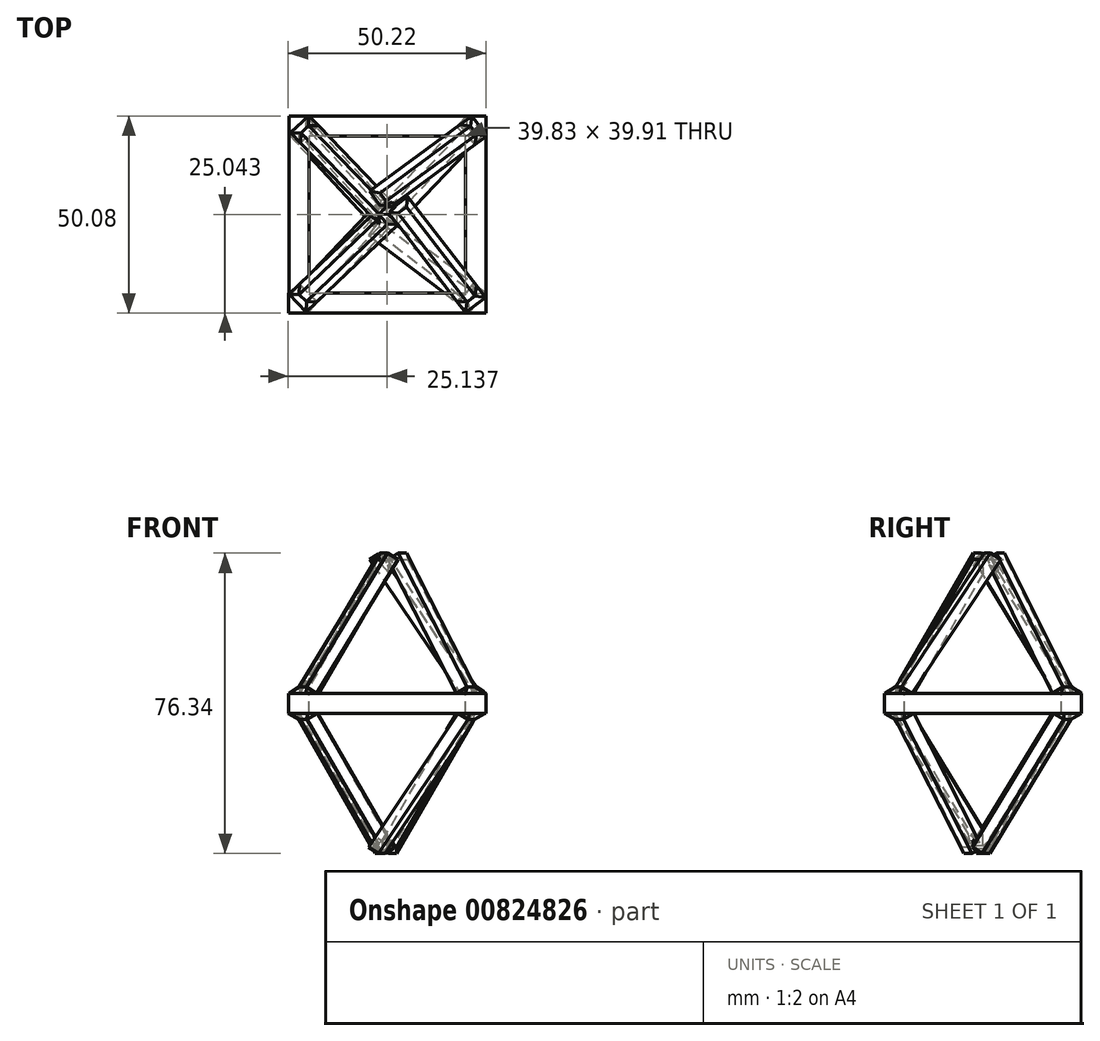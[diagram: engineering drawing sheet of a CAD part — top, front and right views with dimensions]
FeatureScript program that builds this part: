
annotation { "Feature Type Name" : "Feature", "Feature Type Description" : "" }
export const myFeature = defineFeature(function(context is Context, id is Id, definition is map)
    precondition{}
    {
        {
            var Q0;
            Q0=qCreatedBy(makeId("Top.planeOp"),FACE);
            var sketch = newSketch(context, id + "F0", { "sketchPlane" : qUnion([Q0])});
            skLineSegment(sketch, "E0.bottom", {"start": v(-22.5, 22.5) * mm, "end": v(22.5, 22.5) * mm});
            skLineSegment(sketch, "E0.top", {"start": v(-22.5, -22.5) * mm, "end": v(22.5, -22.5) * mm});
            skLineSegment(sketch, "E0.left", {"start": v(-22.5, 22.5) * mm, "end": v(-22.5, -22.5) * mm});
            skLineSegment(sketch, "E0.right", {"start": v(22.5, 22.5) * mm, "end": v(22.5, -22.5) * mm});
            skPoint(sketch, "E0.middle", {"position": v(0, 0) * mm});
            skSolve(sketch);
        }
        {
            var Q0;
            Q0=sQuery(id+"F0.wireOp",EDGE,"E0.left");
            extrude(context, id + "F1", {"bodyType" : ToolBodyType.SURFACE, "surfaceEntities" : qUnion([Q0]), "depth" : 5.08 * mm, "offsetDistance" : 25.4 * mm});
        }
        {
            var Q0;
            Q0=makeQuery(id+"F1.opExtrude","SWEPT_FACE",FACE,{"disambiguationData":[OSD([sQuery(id+"F0.wireOp",EDGE,"E0.left")])]});
            extrude(context, id + "F2", {"entities" : qUnion([Q0]), "depth" : 5.08 * mm, "offsetDistance" : 25.4 * mm});
        }
        {
            var Q0;
            Q0=makeQuery(id+"F1.opExtrude","SWEPT_FACE",FACE,{"disambiguationData":[OSD([sQuery(id+"F0.wireOp",EDGE,"E0.left")])]});
            var sketch = newSketch(context, id + "F3", { "sketchPlane" : qUnion([Q0])});
            skLineSegment(sketch, "E1", {"start": v(-22.5, 0) * mm, "end": v(-17.42, 0) * mm});
            skLineSegment(sketch, "E2", {"start": v(-17.42, 0) * mm, "end": v(-17.42, 5.08) * mm});
            skLineSegment(sketch, "E3", {"start": v(-17.42, 5.08) * mm, "end": v(-22.5, 5.08) * mm});
            skLineSegment(sketch, "E4", {"start": v(-22.5, 5.08) * mm, "end": v(-22.5, 0) * mm});
            skSolve(sketch);
        }
        {
            var Q0;
            Q0=makeQuery(id+"F3.imprint","IMPRINT",FACE,{"disambiguationData":[TD([[makeQuery(id+"F3.imprint","IMPRINT",EDGE,{"derivedFrom":sQuery(id+"F3.wireOp",EDGE,"E1")}),1.0]])]});
            extrude(context, id + "F4", {"entities" : qUnion([Q0]), "operationType" : NewBodyOperationType.ADD, "oppositeDirection" : true, "depth" : 45 * mm, "offsetDistance" : 25.4 * mm});
        }
        {
            var Q0;
            Q0=makeQuery(id+"F4.opExtrude","SWEPT_FACE",FACE,{"disambiguationData":[OSD([sQuery(id+"F3.wireOp",EDGE,"E2")])]});
            var sketch = newSketch(context, id + "F5", { "sketchPlane" : qUnion([Q0])});
            skLineSegment(sketch, "E5", {"start": v(22.5, 0) * mm, "end": v(17.33, 0) * mm});
            skLineSegment(sketch, "E6", {"start": v(17.33, 0) * mm, "end": v(17.33, 5.08) * mm});
            skLineSegment(sketch, "E7", {"start": v(17.33, 5.08) * mm, "end": v(22.5, 5.08) * mm});
            skLineSegment(sketch, "E8", {"start": v(22.5, 5.08) * mm, "end": v(22.5, 0) * mm});
            skSolve(sketch);
        }
        {
            var Q0;
            Q0=makeQuery(id+"F5.imprint","IMPRINT",FACE,{"disambiguationData":[TD([[makeQuery(id+"F5.imprint","IMPRINT",EDGE,{"derivedFrom":sQuery(id+"F5.wireOp",EDGE,"E5")}),-1.0]])]});
            extrude(context, id + "F6", {"entities" : qUnion([Q0]), "operationType" : NewBodyOperationType.ADD, "depth" : 45 * mm, "offsetDistance" : 25.4 * mm});
        }
        {
            var Q0;
            Q0=makeQuery(id+"F6.opExtrude","SWEPT_FACE",FACE,{"disambiguationData":[OSD([sQuery(id+"F5.wireOp",EDGE,"E6")])]});
            var sketch = newSketch(context, id + "F7", { "sketchPlane" : qUnion([Q0])});
            skLineSegment(sketch, "E9", {"start": v(27.58, 0) * mm, "end": v(22.5, 0) * mm});
            skLineSegment(sketch, "E10", {"start": v(22.5, 0) * mm, "end": v(22.5, 5.08) * mm});
            skLineSegment(sketch, "E11", {"start": v(22.5, 5.08) * mm, "end": v(27.58, 5.08) * mm});
            skLineSegment(sketch, "E12", {"start": v(27.58, 5.08) * mm, "end": v(27.58, 0) * mm});
            skSolve(sketch);
        }
        {
            var Q0;
            Q0=makeQuery(id+"F7.imprint","IMPRINT",FACE,{"disambiguationData":[TD([[makeQuery(id+"F7.imprint","IMPRINT",EDGE,{"derivedFrom":sQuery(id+"F7.wireOp",EDGE,"E9")}),-1.0]])]});
            extrude(context, id + "F8", {"entities" : qUnion([Q0]), "operationType" : NewBodyOperationType.ADD, "depth" : 45 * mm, "offsetDistance" : 25.4 * mm});
        }
        {
            var Q0;
            {var subQ0=sQuery(id+"F0.wireOp",EDGE,"E0.left");Q0=makeQuery(id+"F8.boolean.opBoolean","MERGE",FACE,{"derivedFrom":[makeQuery(id+"F6.boolean.opBoolean","MERGE",FACE,{"derivedFrom":[makeQuery(id+"F4.boolean.opBoolean","MERGE",FACE,{"derivedFrom":[makeQuery(id+"F2.opExtrude","SWEPT_FACE",FACE,{"disambiguationData":[OSD([subQ0]),TDD([makeQuery(id+"F1.opExtrude","CAP_EDGE",EDGE,{"disambiguationData":[OSD([subQ0])],"isStart":false})])]}),makeQuery(id+"F4.opExtrude","SWEPT_FACE",FACE,{"disambiguationData":[OSD([sQuery(id+"F3.wireOp",EDGE,"E3")])]})]}),makeQuery(id+"F6.opExtrude","SWEPT_FACE",FACE,{"disambiguationData":[OSD([sQuery(id+"F5.wireOp",EDGE,"E7")])]})]}),makeQuery(id+"F8.opExtrude","SWEPT_FACE",FACE,{"disambiguationData":[OSD([sQuery(id+"F7.wireOp",EDGE,"E11")])]})]});}
            var sketch = newSketch(context, id + "F9", { "sketchPlane" : qUnion([Q0])});
            skLineSegment(sketch, "E13", {"start": v(20.1, -20.6) * mm, "end": v(15.06, -24.5) * mm});
            skLineSegment(sketch, "E14", {"start": v(15.06, -24.5) * mm, "end": v(17.36, -27.47) * mm});
            skLineSegment(sketch, "E15", {"start": v(17.36, -27.47) * mm, "end": v(22.38, -23.59) * mm});
            skLineSegment(sketch, "E16", {"start": v(22.38, -23.59) * mm, "end": v(20.1, -20.6) * mm});
            skSolve(sketch);
        }
        {
            var Q0;
            Q0=makeQuery(id+"F9.imprint","IMPRINT",FACE,{"disambiguationData":[TD([[makeQuery(id+"F9.imprint","IMPRINT",EDGE,{"derivedFrom":sQuery(id+"F9.wireOp",EDGE,"E13")}),1.0]])]});
            extrude(context, id + "F10", {"entities" : qUnion([Q0]), "operationType" : NewBodyOperationType.ADD, "depth" : 5.08 * mm, "offsetDistance" : 25.4 * mm, "hasDraft" : true, "draftAngle" : 50 * degree, "draftPullDirection" : true});
        }
        {
            var Q0;
            Q0=makeQuery(id+"F10.opExtrude","SWEPT_FACE",FACE,{"disambiguationData":[OSD([sQuery(id+"F9.wireOp",EDGE,"E13")])]});
            extrude(context, id + "F11", {"entities" : qUnion([Q0]), "operationType" : NewBodyOperationType.ADD, "depth" : 44.45 * mm, "offsetDistance" : 25.4 * mm});
        }
        {
            var Q0;
            {var subQ0=sQuery(id+"F0.wireOp",EDGE,"E0.left");Q0=makeQuery(id+"F8.boolean.opBoolean","MERGE",FACE,{"derivedFrom":[makeQuery(id+"F6.boolean.opBoolean","MERGE",FACE,{"derivedFrom":[makeQuery(id+"F4.boolean.opBoolean","MERGE",FACE,{"derivedFrom":[makeQuery(id+"F2.opExtrude","SWEPT_FACE",FACE,{"disambiguationData":[OSD([subQ0]),TDD([makeQuery(id+"F1.opExtrude","CAP_EDGE",EDGE,{"disambiguationData":[OSD([subQ0])],"isStart":false})])]}),makeQuery(id+"F4.opExtrude","SWEPT_FACE",FACE,{"disambiguationData":[OSD([sQuery(id+"F3.wireOp",EDGE,"E3")])]})]}),makeQuery(id+"F6.opExtrude","SWEPT_FACE",FACE,{"disambiguationData":[OSD([sQuery(id+"F5.wireOp",EDGE,"E7")])]})]}),makeQuery(id+"F8.opExtrude","SWEPT_FACE",FACE,{"disambiguationData":[OSD([sQuery(id+"F7.wireOp",EDGE,"E11")])]})]});}
            var sketch = newSketch(context, id + "F12", { "sketchPlane" : qUnion([Q0])});
            skLineSegment(sketch, "E17", {"start": v(-24.86, -20.16) * mm, "end": v(-20.48, -24.76) * mm});
            skLineSegment(sketch, "E18", {"start": v(-20.48, -24.76) * mm, "end": v(-23.2, -27.35) * mm});
            skLineSegment(sketch, "E19", {"start": v(-23.2, -27.35) * mm, "end": v(-27.58, -22.75) * mm});
            skLineSegment(sketch, "E20", {"start": v(-27.58, -22.75) * mm, "end": v(-24.86, -20.16) * mm});
            skSolve(sketch);
        }
        {
            var Q0;
            Q0=makeQuery(id+"F12.imprint","IMPRINT",FACE,{"disambiguationData":[TD([[makeQuery(id+"F12.imprint","IMPRINT",EDGE,{"derivedFrom":sQuery(id+"F12.wireOp",EDGE,"E17")}),-1.0]])]});
            extrude(context, id + "F13", {"entities" : qUnion([Q0]), "operationType" : NewBodyOperationType.ADD, "depth" : 5.08 * mm, "offsetDistance" : 25.4 * mm, "hasDraft" : true, "draftAngle" : 50 * degree, "draftPullDirection" : true});
        }
        {
            var Q0;
            Q0=makeQuery(id+"F13.opExtrude","SWEPT_FACE",FACE,{"disambiguationData":[OSD([sQuery(id+"F12.wireOp",EDGE,"E17")])]});
            extrude(context, id + "F14", {"entities" : qUnion([Q0]), "operationType" : NewBodyOperationType.ADD, "depth" : 44.45 * mm, "offsetDistance" : 25.4 * mm});
        }
        {
            var Q0;
            {var subQ0=sQuery(id+"F0.wireOp",EDGE,"E0.left");Q0=makeQuery(id+"F8.boolean.opBoolean","MERGE",FACE,{"derivedFrom":[makeQuery(id+"F6.boolean.opBoolean","MERGE",FACE,{"derivedFrom":[makeQuery(id+"F4.boolean.opBoolean","MERGE",FACE,{"derivedFrom":[makeQuery(id+"F2.opExtrude","SWEPT_FACE",FACE,{"disambiguationData":[OSD([subQ0]),TDD([makeQuery(id+"F1.opExtrude","CAP_EDGE",EDGE,{"disambiguationData":[OSD([subQ0])],"isStart":false})])]}),makeQuery(id+"F4.opExtrude","SWEPT_FACE",FACE,{"disambiguationData":[OSD([sQuery(id+"F3.wireOp",EDGE,"E3")])]})]}),makeQuery(id+"F6.opExtrude","SWEPT_FACE",FACE,{"disambiguationData":[OSD([sQuery(id+"F5.wireOp",EDGE,"E7")])]})]}),makeQuery(id+"F8.opExtrude","SWEPT_FACE",FACE,{"disambiguationData":[OSD([sQuery(id+"F7.wireOp",EDGE,"E11")])]})]});}
            var sketch = newSketch(context, id + "F15", { "sketchPlane" : qUnion([Q0])});
            skLineSegment(sketch, "E21", {"start": v(15.94, 20.27) * mm, "end": v(19.7, 15.16) * mm});
            skLineSegment(sketch, "E22", {"start": v(19.7, 15.16) * mm, "end": v(22.73, 17.38) * mm});
            skLineSegment(sketch, "E23", {"start": v(22.73, 17.38) * mm, "end": v(18.97, 22.5) * mm});
            skLineSegment(sketch, "E24", {"start": v(18.97, 22.5) * mm, "end": v(15.94, 20.27) * mm});
            skSolve(sketch);
        }
        {
            var Q0;
            {var subQ8=sQuery(id+"F15.wireOp",EDGE,"E21");Q0=makeQuery(id+"F15.imprint","IMPRINT",FACE,{"disambiguationData":[TD([[makeQuery(id+"F15.imprint","IMPRINT",EDGE,{"derivedFrom":subQ8}),1.0]])]});}
            extrude(context, id + "F16", {"entities" : qUnion([Q0]), "operationType" : NewBodyOperationType.ADD, "depth" : 5.08 * mm, "offsetDistance" : 25.4 * mm, "hasDraft" : true, "draftAngle" : 50 * degree, "draftPullDirection" : true});
        }
        {
            var Q0;
            Q0=makeQuery(id+"F16.opExtrude","SWEPT_FACE",FACE,{"disambiguationData":[OSD([sQuery(id+"F15.wireOp",EDGE,"E21")])]});
            extrude(context, id + "F17", {"entities" : qUnion([Q0]), "operationType" : NewBodyOperationType.ADD, "depth" : 44.45 * mm, "offsetDistance" : 25.4 * mm});
        }
        {
            var Q0;
            {var subQ0=sQuery(id+"F9.wireOp",EDGE,"E16");var subQ1=sQuery(id+"F0.wireOp",EDGE,"E0.left");var subQ2=sQuery(id+"F9.wireOp",EDGE,"E13");var subQ3=makeQuery(id+"F2.opExtrude","SWEPT_FACE",FACE,{"disambiguationData":[OSD([subQ1]),TDD([makeQuery(id+"F1.opExtrude","CAP_EDGE",EDGE,{"disambiguationData":[OSD([subQ1])],"isStart":false})])]});var subQ4=sQuery(id+"F7.wireOp",EDGE,"E12");var subQ5=sQuery(id+"F7.wireOp",EDGE,"E11");var subQ6=makeQuery(id+"F8.opExtrude","SWEPT_FACE",FACE,{"disambiguationData":[OSD([subQ5])]});var subQ7=sQuery(id+"F7.wireOp",EDGE,"E10");var subQ8=sQuery(id+"F5.wireOp",EDGE,"E8");var subQ9=sQuery(id+"F12.wireOp",EDGE,"E18");var subQ10=sQuery(id+"F9.wireOp",EDGE,"E14");var subQ11=sQuery(id+"F3.wireOp",EDGE,"E3");var subQ12=makeQuery(id+"F4.opExtrude","SWEPT_FACE",FACE,{"disambiguationData":[OSD([subQ11])]});var subQ13=sQuery(id+"F5.wireOp",EDGE,"E7");var subQ14=makeQuery(id+"F6.opExtrude","SWEPT_FACE",FACE,{"disambiguationData":[OSD([subQ13])]});var subQ15=sQuery(id+"F3.wireOp",EDGE,"E2");var subQ16=sQuery(id+"F3.wireOp",EDGE,"E4");var subQ17=sQuery(id+"F5.wireOp",EDGE,"E6");var subQ18=sQuery(id+"F12.wireOp",EDGE,"E20");var subQ19=sQuery(id+"F12.wireOp",EDGE,"E17");Q0=makeQuery(id+"F16.boolean.opBoolean","SPLIT",FACE,{"disambiguationData":[TD([makeQuery(id+"F2.opExtrude","SWEPT_FACE",FACE,{"disambiguationData":[OSD([sQuery(id+"F0.wireOp",VERTEX,"E0.left.start")])]}),subQ3,makeQuery(id+"F2.opExtrude","CAP_FACE",FACE,{"disambiguationData":[OSD([subQ1])],"isStart":true}),makeQuery(id+"F2.opExtrude","CAP_FACE",FACE,{"disambiguationData":[OSD([subQ1])],"isStart":false}),makeQuery(id+"F4.opExtrude","CAP_FACE",FACE,{"disambiguationData":[OSD([sQuery(id+"F3.wireOp",EDGE,"E1"),subQ15,subQ11,subQ16])],"isStart":false}),makeQuery(id+"F4.opExtrude","SWEPT_FACE",FACE,{"disambiguationData":[OSD([subQ15])]}),subQ12,makeQuery(id+"F4.opExtrude","SWEPT_FACE",FACE,{"disambiguationData":[OSD([subQ16])]}),makeQuery(id+"F6.opExtrude","CAP_FACE",FACE,{"disambiguationData":[OSD([sQuery(id+"F5.wireOp",EDGE,"E5"),subQ17,subQ13,subQ8])],"isStart":false}),makeQuery(id+"F6.opExtrude","SWEPT_FACE",FACE,{"disambiguationData":[OSD([subQ17])]}),subQ14,makeQuery(id+"F6.opExtrude","SWEPT_FACE",FACE,{"disambiguationData":[OSD([subQ8])]}),makeQuery(id+"F8.opExtrude","CAP_FACE",FACE,{"disambiguationData":[OSD([sQuery(id+"F7.wireOp",EDGE,"E9"),subQ7,subQ5,subQ4])],"isStart":false}),makeQuery(id+"F8.opExtrude","SWEPT_FACE",FACE,{"disambiguationData":[OSD([subQ7])]}),subQ6,makeQuery(id+"F8.opExtrude","SWEPT_FACE",FACE,{"disambiguationData":[OSD([subQ4])]}),makeQuery(id+"F10.opExtrude","SWEPT_FACE",FACE,{"disambiguationData":[OSD([subQ10])]}),makeQuery(id+"F10.opExtrude","SWEPT_FACE",FACE,{"disambiguationData":[OSD([sQuery(id+"F9.wireOp",EDGE,"E15")])]}),makeQuery(id+"F10.opExtrude","SWEPT_FACE",FACE,{"disambiguationData":[OSD([subQ0])]}),makeQuery(id+"F11.opExtrude","SWEPT_FACE",FACE,{"disambiguationData":[OSD([subQ2,subQ0])]}),makeQuery(id+"F11.opExtrude","SWEPT_FACE",FACE,{"disambiguationData":[OSD([subQ2,subQ10])]}),makeQuery(id+"F11.opExtrude","SWEPT_FACE",FACE,{"disambiguationData":[OSD([subQ2])]}),makeQuery(id+"F13.opExtrude","SWEPT_FACE",FACE,{"disambiguationData":[OSD([subQ9])]}),makeQuery(id+"F13.opExtrude","SWEPT_FACE",FACE,{"disambiguationData":[OSD([sQuery(id+"F12.wireOp",EDGE,"E19")])]}),makeQuery(id+"F13.opExtrude","SWEPT_FACE",FACE,{"disambiguationData":[OSD([subQ18])]}),makeQuery(id+"F14.opExtrude","SWEPT_FACE",FACE,{"disambiguationData":[OSD([subQ19,subQ18])]}),makeQuery(id+"F14.opExtrude","SWEPT_FACE",FACE,{"disambiguationData":[OSD([subQ19,subQ9])]}),makeQuery(id+"F14.opExtrude","SWEPT_FACE",FACE,{"disambiguationData":[OSD([subQ19])]}),makeQuery(id+"F16.opExtrude","SWEPT_FACE",FACE,{"disambiguationData":[OSD([sQuery(id+"F15.wireOp",EDGE,"E21")])]}),makeQuery(id+"F16.opExtrude","SWEPT_FACE",FACE,{"disambiguationData":[OSD([sQuery(id+"F15.wireOp",EDGE,"E22")])]}),makeQuery(id+"F16.opExtrude","SWEPT_FACE",FACE,{"disambiguationData":[OSD([sQuery(id+"F15.wireOp",EDGE,"E23")])]}),makeQuery(id+"F16.opExtrude","SWEPT_FACE",FACE,{"disambiguationData":[OSD([sQuery(id+"F15.wireOp",EDGE,"E24")])]}),makeQuery(id+"F16.opExtrude","SWEPT_FACE",FACE,{"disambiguationData":[OSD([subQ11,subQ13,subQ8])]})])],"derivedFrom":makeQuery(id+"F8.boolean.opBoolean","MERGE",FACE,{"derivedFrom":[makeQuery(id+"F6.boolean.opBoolean","MERGE",FACE,{"derivedFrom":[makeQuery(id+"F4.boolean.opBoolean","MERGE",FACE,{"derivedFrom":[subQ3,subQ12]}),subQ14]}),subQ6]})});}
            var sketch = newSketch(context, id + "F18", { "sketchPlane" : qUnion([Q0])});
            skLineSegment(sketch, "E25", {"start": v(-24.55, 15.6) * mm, "end": v(-19.98, 20) * mm});
            skLineSegment(sketch, "E26", {"start": v(-19.98, 20) * mm, "end": v(-22.5, 22.61) * mm});
            skLineSegment(sketch, "E27", {"start": v(-22.5, 22.61) * mm, "end": v(-27.07, 18.2) * mm});
            skLineSegment(sketch, "E28", {"start": v(-27.07, 18.2) * mm, "end": v(-24.55, 15.6) * mm});
            skSolve(sketch);
        }
        {
            var Q0;
            {var subQ9=sQuery(id+"F18.wireOp",EDGE,"E25");Q0=makeQuery(id+"F18.imprint","IMPRINT",FACE,{"disambiguationData":[TD([[makeQuery(id+"F18.imprint","IMPRINT",EDGE,{"derivedFrom":subQ9}),1.0]])]});}
            extrude(context, id + "F19", {"entities" : qUnion([Q0]), "operationType" : NewBodyOperationType.ADD, "depth" : 5.08 * mm, "offsetDistance" : 25.4 * mm, "hasDraft" : true, "draftAngle" : 50 * degree, "draftPullDirection" : true});
        }
        {
            var Q0;
            Q0=makeQuery(id+"F19.opExtrude","SWEPT_FACE",FACE,{"disambiguationData":[OSD([sQuery(id+"F18.wireOp",EDGE,"E25")])]});
            extrude(context, id + "F20", {"entities" : qUnion([Q0]), "operationType" : NewBodyOperationType.ADD, "depth" : 44.45 * mm, "offsetDistance" : 25.4 * mm});
        }
        {
            var Q0;
            {var subQ0=sQuery(id+"F0.wireOp",EDGE,"E0.left");Q0=makeQuery(id+"F8.boolean.opBoolean","MERGE",FACE,{"derivedFrom":[makeQuery(id+"F6.boolean.opBoolean","MERGE",FACE,{"derivedFrom":[makeQuery(id+"F4.boolean.opBoolean","MERGE",FACE,{"derivedFrom":[makeQuery(id+"F2.opExtrude","SWEPT_FACE",FACE,{"disambiguationData":[OSD([subQ0]),TDD([makeQuery(id+"F1.opExtrude","CAP_EDGE",EDGE,{"disambiguationData":[OSD([subQ0])],"isStart":true})])]}),makeQuery(id+"F4.opExtrude","SWEPT_FACE",FACE,{"disambiguationData":[OSD([sQuery(id+"F3.wireOp",EDGE,"E1")])]})]}),makeQuery(id+"F6.opExtrude","SWEPT_FACE",FACE,{"disambiguationData":[OSD([sQuery(id+"F5.wireOp",EDGE,"E5")])]})]}),makeQuery(id+"F8.opExtrude","SWEPT_FACE",FACE,{"disambiguationData":[OSD([sQuery(id+"F7.wireOp",EDGE,"E9")])]})]});}
            var sketch = newSketch(context, id + "F21", { "sketchPlane" : qUnion([Q0])});
            skLineSegment(sketch, "E29", {"start": v(-24.83, 20.45) * mm, "end": v(-20.22, 24.82) * mm});
            skLineSegment(sketch, "E30", {"start": v(-20.22, 24.82) * mm, "end": v(-22.81, 27.55) * mm});
            skLineSegment(sketch, "E31", {"start": v(-22.81, 27.55) * mm, "end": v(-27.42, 23.18) * mm});
            skLineSegment(sketch, "E32", {"start": v(-27.42, 23.18) * mm, "end": v(-24.83, 20.45) * mm});
            skSolve(sketch);
        }
        {
            var Q0;
            Q0=makeQuery(id+"F21.imprint","IMPRINT",FACE,{"disambiguationData":[TD([[makeQuery(id+"F21.imprint","IMPRINT",EDGE,{"derivedFrom":sQuery(id+"F21.wireOp",EDGE,"E29")}),1.0]])]});
            extrude(context, id + "F22", {"entities" : qUnion([Q0]), "operationType" : NewBodyOperationType.ADD, "depth" : 5.08 * mm, "offsetDistance" : 25.4 * mm, "hasDraft" : true, "draftAngle" : 50 * degree, "draftPullDirection" : true});
        }
        {
            var Q0;
            Q0=makeQuery(id+"F22.opExtrude","SWEPT_FACE",FACE,{"disambiguationData":[OSD([sQuery(id+"F21.wireOp",EDGE,"E29")])]});
            extrude(context, id + "F23", {"entities" : qUnion([Q0]), "operationType" : NewBodyOperationType.ADD, "depth" : 44.45 * mm, "offsetDistance" : 25.4 * mm});
        }
        {
            var Q0;
            {var subQ0=sQuery(id+"F0.wireOp",EDGE,"E0.left");Q0=makeQuery(id+"F8.boolean.opBoolean","MERGE",FACE,{"derivedFrom":[makeQuery(id+"F6.boolean.opBoolean","MERGE",FACE,{"derivedFrom":[makeQuery(id+"F4.boolean.opBoolean","MERGE",FACE,{"derivedFrom":[makeQuery(id+"F2.opExtrude","SWEPT_FACE",FACE,{"disambiguationData":[OSD([subQ0]),TDD([makeQuery(id+"F1.opExtrude","CAP_EDGE",EDGE,{"disambiguationData":[OSD([subQ0])],"isStart":true})])]}),makeQuery(id+"F4.opExtrude","SWEPT_FACE",FACE,{"disambiguationData":[OSD([sQuery(id+"F3.wireOp",EDGE,"E1")])]})]}),makeQuery(id+"F6.opExtrude","SWEPT_FACE",FACE,{"disambiguationData":[OSD([sQuery(id+"F5.wireOp",EDGE,"E5")])]})]}),makeQuery(id+"F8.opExtrude","SWEPT_FACE",FACE,{"disambiguationData":[OSD([sQuery(id+"F7.wireOp",EDGE,"E9")])]})]});}
            var sketch = newSketch(context, id + "F24", { "sketchPlane" : qUnion([Q0])});
            skLineSegment(sketch, "E33", {"start": v(-25.16, -15.16) * mm, "end": v(-20.5, -19.48) * mm});
            skLineSegment(sketch, "E34", {"start": v(-20.5, -19.48) * mm, "end": v(-23.07, -22.23) * mm});
            skLineSegment(sketch, "E35", {"start": v(-23.07, -22.23) * mm, "end": v(-27.72, -17.91) * mm});
            skLineSegment(sketch, "E36", {"start": v(-27.72, -17.91) * mm, "end": v(-25.16, -15.16) * mm});
            skSolve(sketch);
        }
        {
            var Q0;
            Q0=qSketchRegion(id+"F24",true);
            extrude(context, id + "F25", {"entities" : qUnion([Q0]), "operationType" : NewBodyOperationType.ADD, "depth" : 5.08 * mm, "offsetDistance" : 25.4 * mm, "hasDraft" : true, "draftAngle" : 50 * degree, "draftPullDirection" : true});
        }
        {
            var Q0;
            Q0=makeQuery(id+"F25.opExtrude","SWEPT_FACE",FACE,{"disambiguationData":[OSD([sQuery(id+"F24.wireOp",EDGE,"E33")])]});
            extrude(context, id + "F26", {"entities" : qUnion([Q0]), "operationType" : NewBodyOperationType.ADD, "depth" : 44.45 * mm, "offsetDistance" : 25.4 * mm});
        }
        {
            var Q0;
            {var subQ0=sQuery(id+"F0.wireOp",EDGE,"E0.left");Q0=makeQuery(id+"F8.boolean.opBoolean","MERGE",FACE,{"derivedFrom":[makeQuery(id+"F6.boolean.opBoolean","MERGE",FACE,{"derivedFrom":[makeQuery(id+"F4.boolean.opBoolean","MERGE",FACE,{"derivedFrom":[makeQuery(id+"F2.opExtrude","SWEPT_FACE",FACE,{"disambiguationData":[OSD([subQ0]),TDD([makeQuery(id+"F1.opExtrude","CAP_EDGE",EDGE,{"disambiguationData":[OSD([subQ0])],"isStart":true})])]}),makeQuery(id+"F4.opExtrude","SWEPT_FACE",FACE,{"disambiguationData":[OSD([sQuery(id+"F3.wireOp",EDGE,"E1")])]})]}),makeQuery(id+"F6.opExtrude","SWEPT_FACE",FACE,{"disambiguationData":[OSD([sQuery(id+"F5.wireOp",EDGE,"E5")])]})]}),makeQuery(id+"F8.opExtrude","SWEPT_FACE",FACE,{"disambiguationData":[OSD([sQuery(id+"F7.wireOp",EDGE,"E9")])]})]});}
            var sketch = newSketch(context, id + "F27", { "sketchPlane" : qUnion([Q0])});
            skLineSegment(sketch, "E37", {"start": v(19.59, -15.35) * mm, "end": v(15, -19.74) * mm});
            skLineSegment(sketch, "E38", {"start": v(15, -19.74) * mm, "end": v(17.6, -22.45) * mm});
            skLineSegment(sketch, "E39", {"start": v(17.6, -22.45) * mm, "end": v(22.19, -18.06) * mm});
            skLineSegment(sketch, "E40", {"start": v(22.19, -18.06) * mm, "end": v(19.59, -15.35) * mm});
            skSolve(sketch);
        }
        {
            var Q0;
            Q0=makeQuery(id+"F27.imprint","IMPRINT",FACE,{"disambiguationData":[TD([[makeQuery(id+"F27.imprint","IMPRINT",EDGE,{"derivedFrom":sQuery(id+"F27.wireOp",EDGE,"E37")}),1.0]])]});
            extrude(context, id + "F28", {"entities" : qUnion([Q0]), "operationType" : NewBodyOperationType.ADD, "depth" : 5.08 * mm, "offsetDistance" : 25.4 * mm, "hasDraft" : true, "draftAngle" : 50 * degree, "draftPullDirection" : true});
        }
        {
            var Q0;
            Q0=makeQuery(id+"F28.opExtrude","SWEPT_FACE",FACE,{"disambiguationData":[OSD([sQuery(id+"F27.wireOp",EDGE,"E37")])]});
            extrude(context, id + "F29", {"entities" : qUnion([Q0]), "operationType" : NewBodyOperationType.ADD, "depth" : 44.45 * mm, "offsetDistance" : 25.4 * mm});
        }
        {
            var Q0;
            {var subQ0=sQuery(id+"F0.wireOp",EDGE,"E0.left");Q0=makeQuery(id+"F8.boolean.opBoolean","MERGE",FACE,{"derivedFrom":[makeQuery(id+"F6.boolean.opBoolean","MERGE",FACE,{"derivedFrom":[makeQuery(id+"F4.boolean.opBoolean","MERGE",FACE,{"derivedFrom":[makeQuery(id+"F2.opExtrude","SWEPT_FACE",FACE,{"disambiguationData":[OSD([subQ0]),TDD([makeQuery(id+"F1.opExtrude","CAP_EDGE",EDGE,{"disambiguationData":[OSD([subQ0])],"isStart":true})])]}),makeQuery(id+"F4.opExtrude","SWEPT_FACE",FACE,{"disambiguationData":[OSD([sQuery(id+"F3.wireOp",EDGE,"E1")])]})]}),makeQuery(id+"F6.opExtrude","SWEPT_FACE",FACE,{"disambiguationData":[OSD([sQuery(id+"F5.wireOp",EDGE,"E5")])]})]}),makeQuery(id+"F8.opExtrude","SWEPT_FACE",FACE,{"disambiguationData":[OSD([sQuery(id+"F7.wireOp",EDGE,"E9")])]})]});}
            var sketch = newSketch(context, id + "F30", { "sketchPlane" : qUnion([Q0])});
            skLineSegment(sketch, "E41", {"start": v(15.37, 25.12) * mm, "end": v(19.22, 20.07) * mm});
            skLineSegment(sketch, "E42", {"start": v(19.22, 20.07) * mm, "end": v(22.2, 22.35) * mm});
            skLineSegment(sketch, "E43", {"start": v(22.2, 22.35) * mm, "end": v(18.36, 27.4) * mm});
            skLineSegment(sketch, "E44", {"start": v(18.36, 27.4) * mm, "end": v(15.37, 25.12) * mm});
            skSolve(sketch);
        }
        {
            var Q0;
            Q0=makeQuery(id+"F30.imprint","IMPRINT",FACE,{"disambiguationData":[TD([[makeQuery(id+"F30.imprint","IMPRINT",EDGE,{"derivedFrom":sQuery(id+"F30.wireOp",EDGE,"E41")}),1.0]])]});
            extrude(context, id + "F31", {"entities" : qUnion([Q0]), "operationType" : NewBodyOperationType.ADD, "depth" : 5.08 * mm, "offsetDistance" : 25.4 * mm, "hasDraft" : true, "draftAngle" : 50 * degree, "draftPullDirection" : true});
        }
        {
            var Q0;
            Q0=makeQuery(id+"F31.opExtrude","SWEPT_FACE",FACE,{"disambiguationData":[OSD([sQuery(id+"F30.wireOp",EDGE,"E41")])]});
            extrude(context, id + "F32", {"entities" : qUnion([Q0]), "operationType" : NewBodyOperationType.ADD, "depth" : 44.45 * mm, "offsetDistance" : 25.4 * mm});
        }
    });
